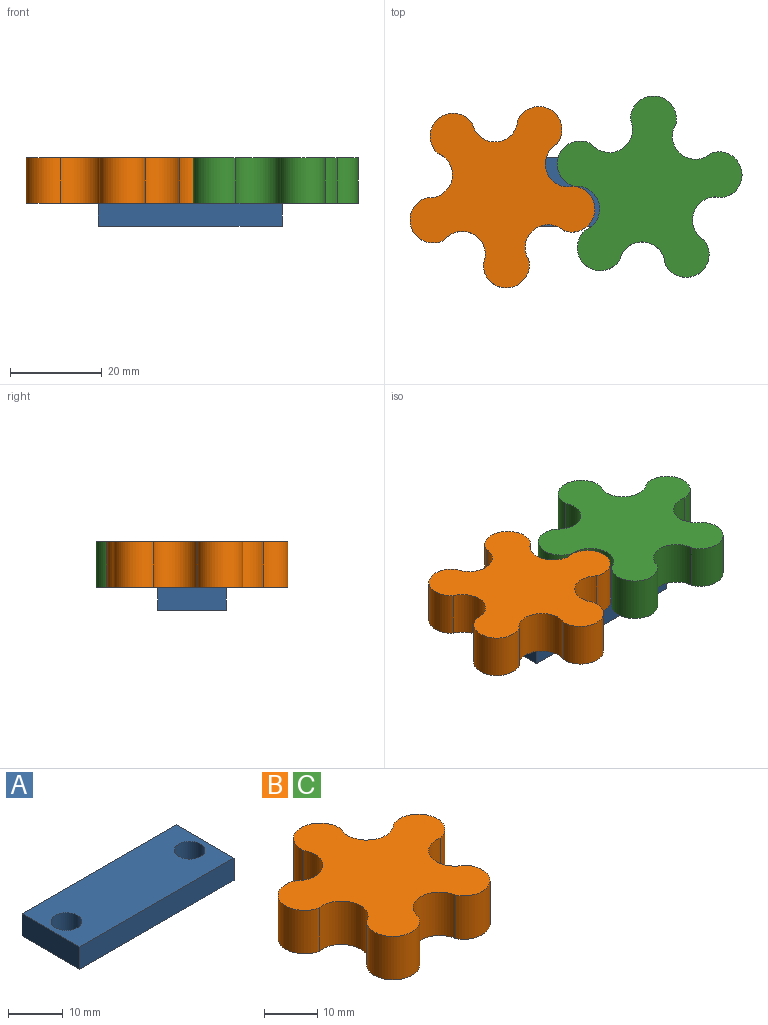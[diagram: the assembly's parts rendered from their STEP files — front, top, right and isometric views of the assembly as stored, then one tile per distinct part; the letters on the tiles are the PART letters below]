
ASSEMBLY  parts=3 mates=2
PART A: 8 faces, bbox 40x15x5 mm
  f0: plane 40x5mm, normal (0,1,0), area 200mm2, adj f1,f4,f6,f7
  f1: plane 15x5mm, normal (-1,0,0), area 75mm2, adj f0,f2,f6,f7
  f2: plane 40x5mm, normal (0,-1,0), area 200mm2, adj f1,f4,f6,f7
  f3: cylinder r=2.81mm len=5.62mm, axis (0,0,-1), area 88.3mm2, adj f6,f7
  f4: plane 15x5mm, normal (1,0,0), area 75mm2, adj f0,f2,f6,f7
  f5: cylinder r=2.81mm len=5.62mm, axis (0,0,-1), area 88.3mm2, adj f6,f7
  f6: plane 40x15mm, normal (0,0,1), area 550.4mm2, adj f0,f1,f2,f3,f4,f5
  f7: plane 40x15mm, normal (0,0,-1), area 550.4mm2, adj f0,f1,f2,f3,f4,f5
PART B: 12 faces, bbox 40.3x38.8x10 mm
  f0: cylinder r=5mm len=10mm, axis (0,0,-1), area 143.8mm2, adj f1,f9,f10,f11
  f1: cylinder r=5mm len=10mm, axis (0,0,-1), area 170.4mm2, adj f0,f2,f10,f11
  f2: cylinder r=5mm len=10mm, axis (0,0,-1), area 143.8mm2, adj f1,f3,f10,f11
  f3: cylinder r=5mm len=10mm, axis (0,0,-1), area 170.4mm2, adj f2,f4,f10,f11
  f4: cylinder r=5mm len=10mm, axis (0,0,-1), area 143.8mm2, adj f3,f5,f10,f11
  f5: cylinder r=5mm len=10mm, axis (0,0,-1), area 170.4mm2, adj f4,f6,f10,f11
  f6: cylinder r=5mm len=10mm, axis (0,0,-1), area 143.8mm2, adj f5,f7,f10,f11
  f7: cylinder r=5mm len=10mm, axis (0,0,-1), area 170.4mm2, adj f6,f8,f10,f11
  f8: cylinder r=5mm len=10mm, axis (0,0,-1), area 143.8mm2, adj f7,f9,f10,f11
  f9: cylinder r=5mm len=10mm, axis (0,0,-1), area 170.4mm2, adj f0,f8,f10,f11
  f10: plane 40.27x38.79mm, normal (0,0,1), area 821.9mm2, adj f0,f1,f2,f3,f4,f5,f6,f7
  f11: plane 40.27x38.79mm, normal (0,0,-1), area 821.9mm2, adj f0,f1,f2,f3,f4,f5,f6,f7
PART C: same geometry as B
PLACE A t=(3.24,2.89,0)mm fixed
PLACE B rot(axis=(0,0,-1),175.5deg) t=(87.34,10.14,15)mm
PLACE C rot(axis=(0.04,1,0),180deg) t=(119.34,4.16,25)mm
MATE revolute B.f11 <-> A.f5  axis (0,0,-1) through (49.05,7.15,15)mm
MATE revolute C.f10 <-> A.f3  axis (0,0,-1) through (81.05,7.15,15)mm
